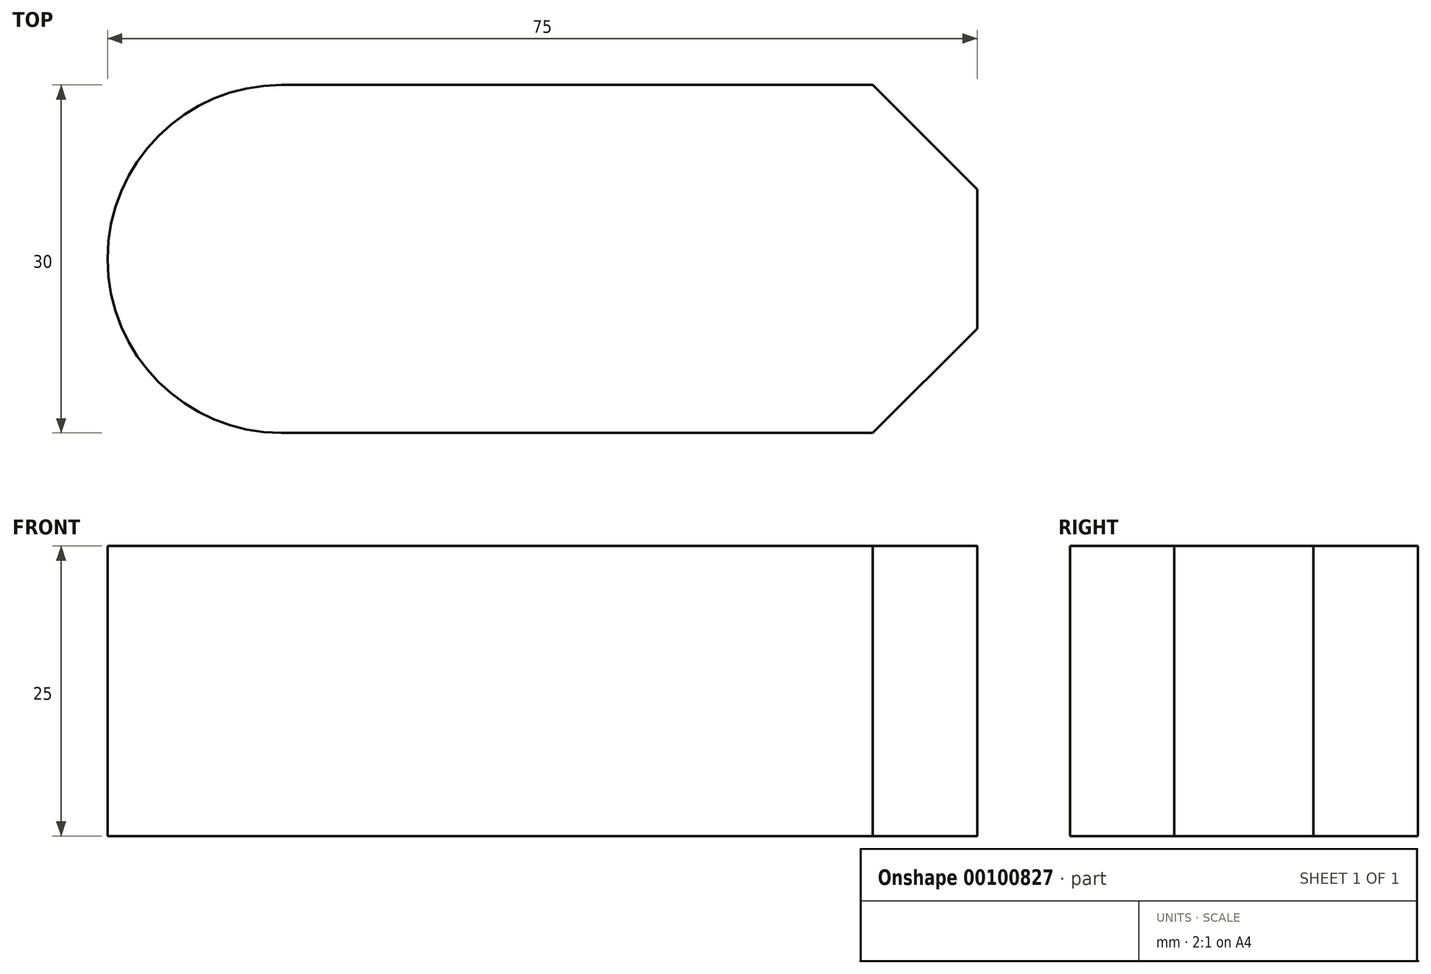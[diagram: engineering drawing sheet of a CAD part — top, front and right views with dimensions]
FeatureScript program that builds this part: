
annotation { "Feature Type Name" : "Feature", "Feature Type Description" : "" }
export const myFeature = defineFeature(function(context is Context, id is Id, definition is map)
    precondition{}
    {
        {
            var Q0;
            Q0=qCreatedBy(makeId("Top.planeOp"),FACE);
            var sketch = newSketch(context, id + "F0", { "sketchPlane" : qUnion([Q0])});
            skLineSegment(sketch, "E0.bottom", {"start": v(0, 0) * mm, "end": v(51, 0) * mm});
            skLineSegment(sketch, "E0.top", {"start": v(0, 30) * mm, "end": v(51, 30) * mm});
            skArc(sketch, "E1", {"start": v(0, 30) * mm, "mid": v(-15, 15) * mm, "end": v(0, 0) * mm});
            skPoint(sketch, "E2.start.orphan", {"position": v(62.03, 0) * mm});
            skLineSegment(sketch, "E3", {"start": v(60, 21) * mm, "end": v(60, 0) * mm});
            skLineSegment(sketch, "E4", {"start": v(60, 21) * mm, "end": v(60, 9) * mm});
            skLineSegment(sketch, "E5", {"start": v(60, 9) * mm, "end": v(51, 0) * mm});
            skLineSegment(sketch, "E6", {"start": v(51, 30) * mm, "end": v(60, 21) * mm});
            skPoint(sketch, "E7.orphan", {"position": v(60, 30) * mm});
            skSolve(sketch);
        }
        {
            var Q0;
            Q0=makeQuery(id+"F0.imprint","IMPRINT",FACE,{"disambiguationData":[TD([[makeQuery(id+"F0.imprint","IMPRINT",EDGE,{"derivedFrom":sQuery(id+"F0.wireOp",EDGE,"E0.bottom")}),1.0]])]});
            extrude(context, id + "F1", {"entities" : qUnion([Q0]), "depth" : 25 * mm});
        }
    });
